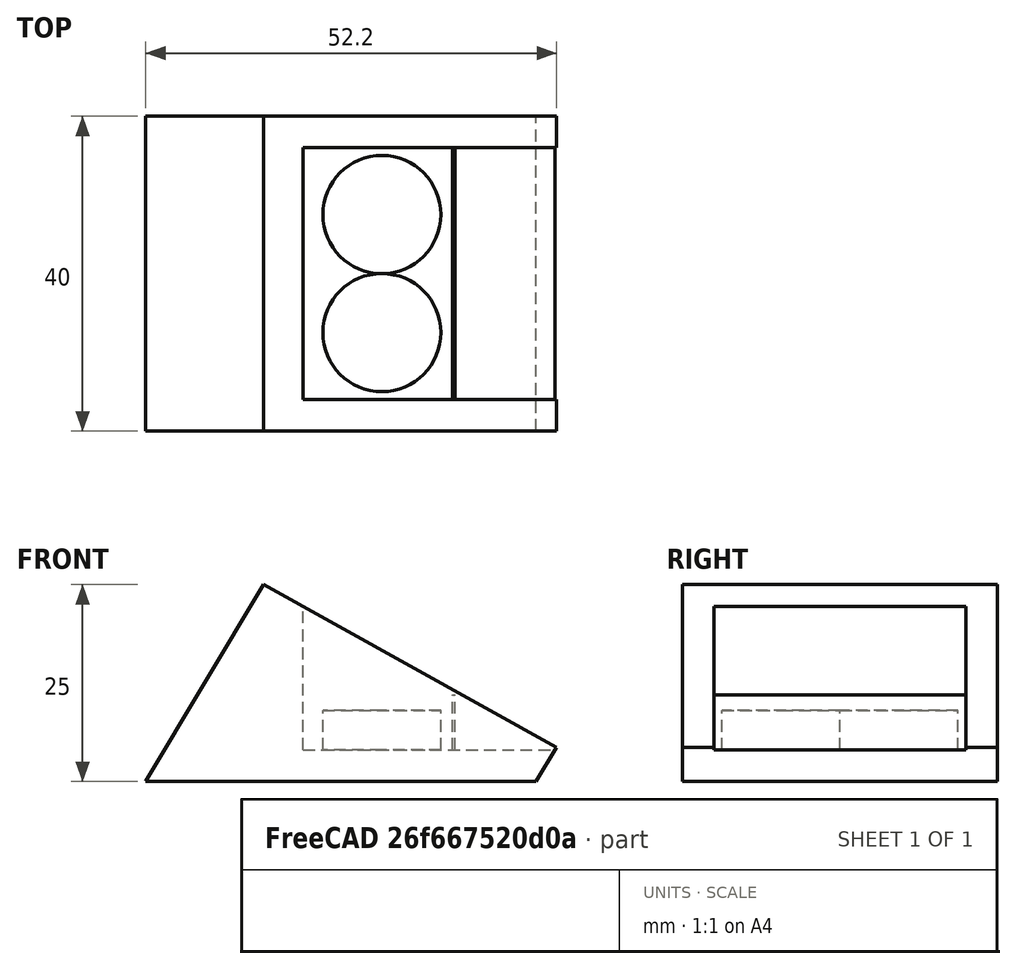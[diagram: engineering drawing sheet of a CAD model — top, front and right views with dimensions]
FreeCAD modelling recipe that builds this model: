
FCSTD DOCUMENT  (FreeCAD 0.18RUnknown)
Label: rfeed
License: All rights reserved
LicenseURL: http://en.wikipedia.org/wiki/All_rights_reserved
objects: Part::Fuse×3, Part::Feature×2, Part::FeaturePython×2, Part::Extrusion×2, Part::Box×2, Part::Cylinder×2, Part::Cut×1, Sketcher::SketchObject×1, PartDesign::Body×1
note: 16 computed .brp shape members not serialized (recipe doc carries the construction recipe); baked Part::Feature solids carry a one-line shape summary decoded from their .brp

FEATURE [Part::Feature] polygon
  shape: bbox 60 x 25 x 2e-07 mm, 1 faces, 0 solids (baked)
FEATURE [Part::FeaturePython] RefineLinearExtrude  # WARN: FeaturePython — macro-defined, semantics opaque (R4)
  Base = -> polygon
FEATURE [Part::Extrusion] LinearExtrude
  Base = -> RefineLinearExtrude
  Dir = (0,0,40)
  DirMode = 0
  FaceMakerClass = Part::FaceMakerBullseye
  LengthFwd = 0
  LengthRev = 0
  Placement = pos=(0,0,0) rot=(1,0,0;1.5708rad)
  Solid = false
  Symmetric = false
FEATURE [Part::Box] cube
  AttacherType = Attacher::AttachEngine3D
  Height = 40
  Length = 60
  Placement = pos=(20,-36,4) rot=(0,0,1;0rad)
  Width = 32
FEATURE [Part::Feature] polygon001
  shape: bbox 60 x 25 x 2e-07 mm, 1 faces, 0 solids (baked)
FEATURE [Part::FeaturePython] RefineLinearExtrude001  # WARN: FeaturePython — macro-defined, semantics opaque (R4)
  Base = -> polygon001
FEATURE [Part::Extrusion] LinearExtrude001
  Base = -> RefineLinearExtrude001
  Dir = (0,0,42)
  DirMode = 0
  FaceMakerClass = Part::FaceMakerBullseye
  LengthFwd = 0
  LengthRev = 0
  Placement = pos=(49,1,-1) rot=(1,0,0;1.5708rad)
  Solid = false
  Symmetric = false
FEATURE [Part::Fuse] union
  Base = -> cube
  Tool = -> LinearExtrude001
FEATURE [Part::Cut] difference
  Base = -> LinearExtrude
  Tool = -> union
FEATURE [Part::Cylinder] cylinder
  Angle = 360
  AttacherType = Attacher::AttachEngine3D
  Height = 5
  Placement = pos=(0,-7.5,0) rot=(0,0,1;0rad)
  Radius = 7.5
FEATURE [Part::Cylinder] cylinder001
  Angle = 360
  AttacherType = Attacher::AttachEngine3D
  Height = 5
  Placement = pos=(0,7.5,0) rot=(0,0,1;0rad)
  Radius = 7.5
FEATURE [Part::Fuse] union001
  Base = -> cylinder
  Tool = -> cylinder001
FEATURE [Part::Box] cube001
  AttacherType = Attacher::AttachEngine3D
  Height = 7
  Length = 0.3
  Placement = pos=(9,-16,0) rot=(0,0,1;0rad)
  Width = 32
FEATURE [Part::Fuse] Matrix_Union
  Base = -> union001
  Placement = pos=(30,-20,4) rot=(0,0,1;0rad)
  Tool = -> cube001
FEATURE [Sketcher::SketchObject] Sketch
  MapMode = 5
  Support = -> [XY_Plane]
FEATURE [PartDesign::Body] Body
  Group = -> [Sketch]
  Origin = -> Origin
